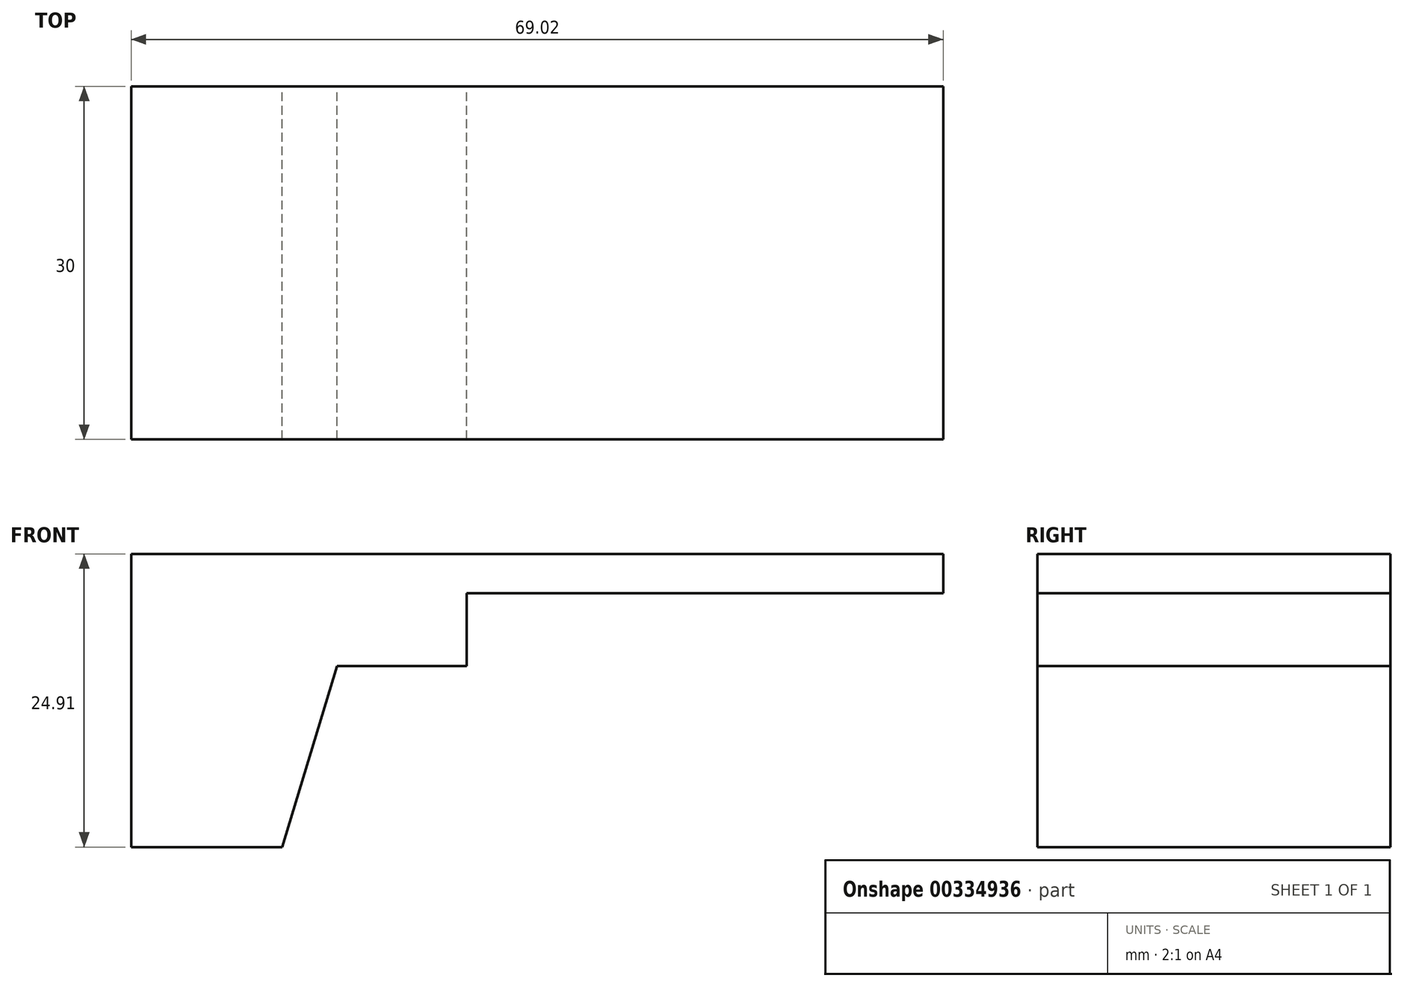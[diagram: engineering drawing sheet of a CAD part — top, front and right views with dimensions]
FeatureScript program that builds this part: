
annotation { "Feature Type Name" : "Feature", "Feature Type Description" : "" }
export const myFeature = defineFeature(function(context is Context, id is Id, definition is map)
    precondition{}
    {
        {
            var Q0;
            Q0=qCreatedBy(makeId("Front.planeOp"),FACE);
            var sketch = newSketch(context, id + "F0", { "sketchPlane" : qUnion([Q0])});
            skLineSegment(sketch, "E0", {"start": v(-33.59, 0) * mm, "end": v(-33.59, 24.91) * mm});
            skLineSegment(sketch, "E1", {"start": v(-33.59, 24.91) * mm, "end": v(35.43, 24.91) * mm});
            skLineSegment(sketch, "E2", {"start": v(35.43, 24.91) * mm, "end": v(35.43, 21.6) * mm});
            skLineSegment(sketch, "E3", {"start": v(35.43, 21.6) * mm, "end": v(-5.07, 21.6) * mm});
            skLineSegment(sketch, "E4", {"start": v(-5.07, 21.6) * mm, "end": v(-5.07, 15.38) * mm});
            skLineSegment(sketch, "E5", {"start": v(-5.07, 15.38) * mm, "end": v(-16.09, 15.38) * mm});
            skLineSegment(sketch, "E6", {"start": v(-16.09, 15.38) * mm, "end": v(-20.74, 0) * mm});
            skLineSegment(sketch, "E7", {"start": v(-20.74, 0) * mm, "end": v(-33.59, 0) * mm});
            skSolve(sketch);
        }
        {
            var Q0;
            Q0 = qSketchRegion(id + "F0", true);
            extrude(context, id + "F1", {"entities" : qUnion([Q0]), "depth" : 30 * mm});
        }
    });
